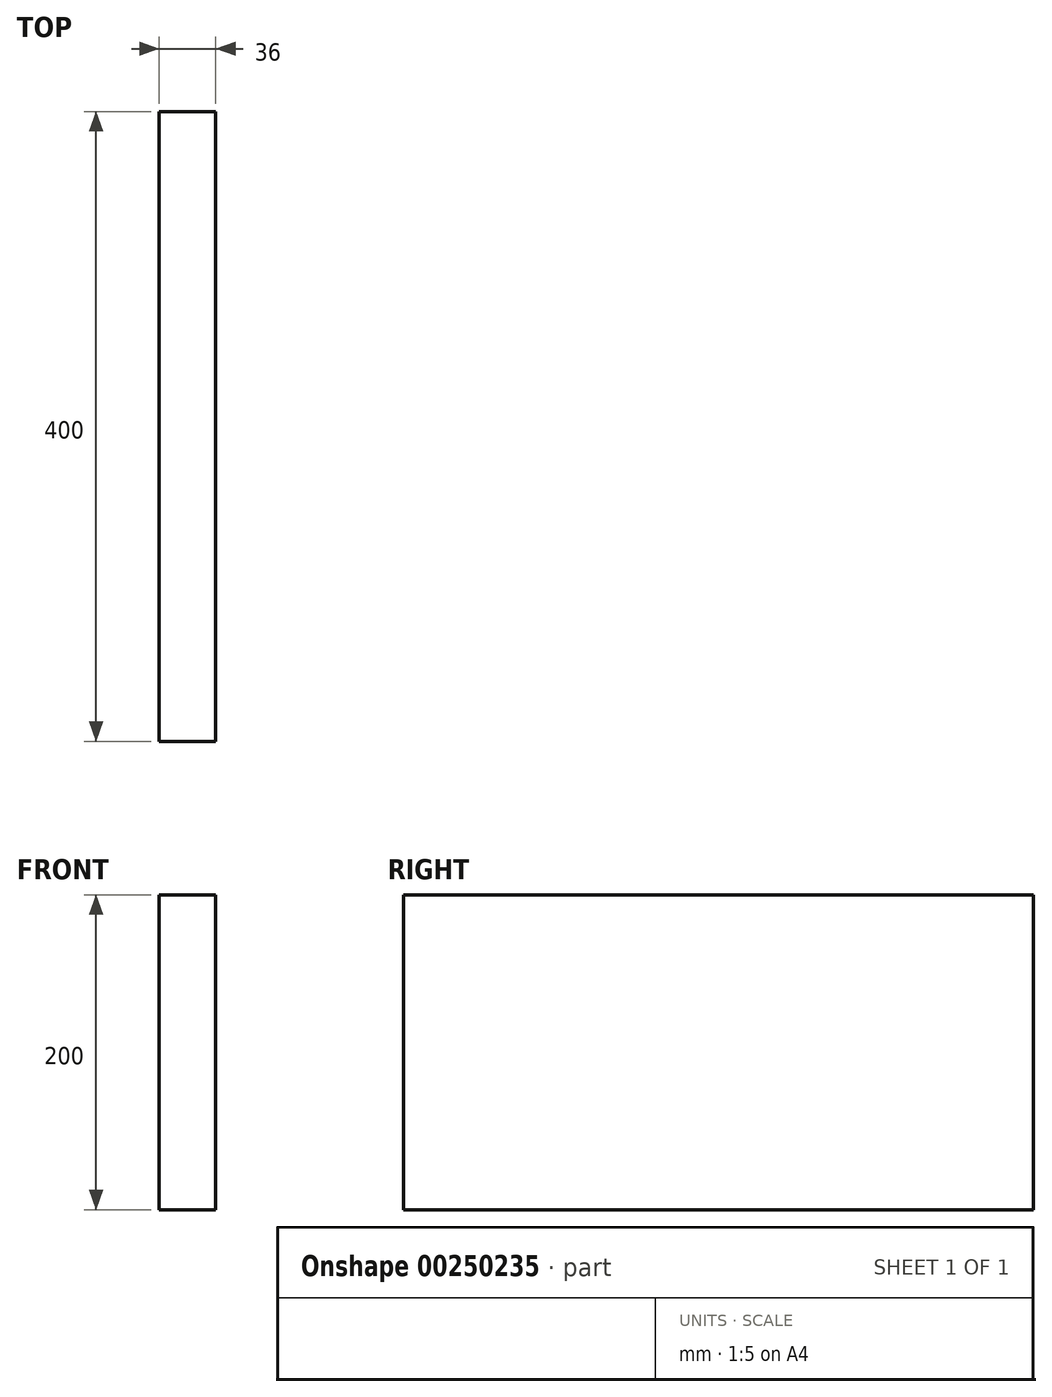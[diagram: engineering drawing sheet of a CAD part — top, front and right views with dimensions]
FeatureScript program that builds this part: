
annotation { "Feature Type Name" : "Feature", "Feature Type Description" : "" }
export const myFeature = defineFeature(function(context is Context, id is Id, definition is map)
    precondition{}
    {
        {
            var Q0;
            Q0=qCreatedBy(makeId("Front.planeOp"),FACE);
            var sketch = newSketch(context, id + "F0", { "sketchPlane" : qUnion([Q0])});
            skLineSegment(sketch, "E0.bottom", {"start": v(-25.14, 100) * mm, "end": v(10.86, 100) * mm});
            skLineSegment(sketch, "E0.top", {"start": v(-25.14, -100) * mm, "end": v(10.86, -100) * mm});
            skLineSegment(sketch, "E0.left", {"start": v(-25.14, 100) * mm, "end": v(-25.14, -100) * mm});
            skLineSegment(sketch, "E0.right", {"start": v(10.86, 100) * mm, "end": v(10.86, -100) * mm});
            skSolve(sketch);
        }
        {
            var Q0;
            Q0=makeQuery(id+"F0.imprint","IMPRINT",FACE,{"disambiguationData":[TD([[makeQuery(id+"F0.imprint","IMPRINT",EDGE,{"derivedFrom":sQuery(id+"F0.wireOp",EDGE,"E0.bottom")}),-1.0]])]});
            extrude(context, id + "F1", {"entities" : qUnion([Q0]), "depth" : 400 * mm});
        }
    });
